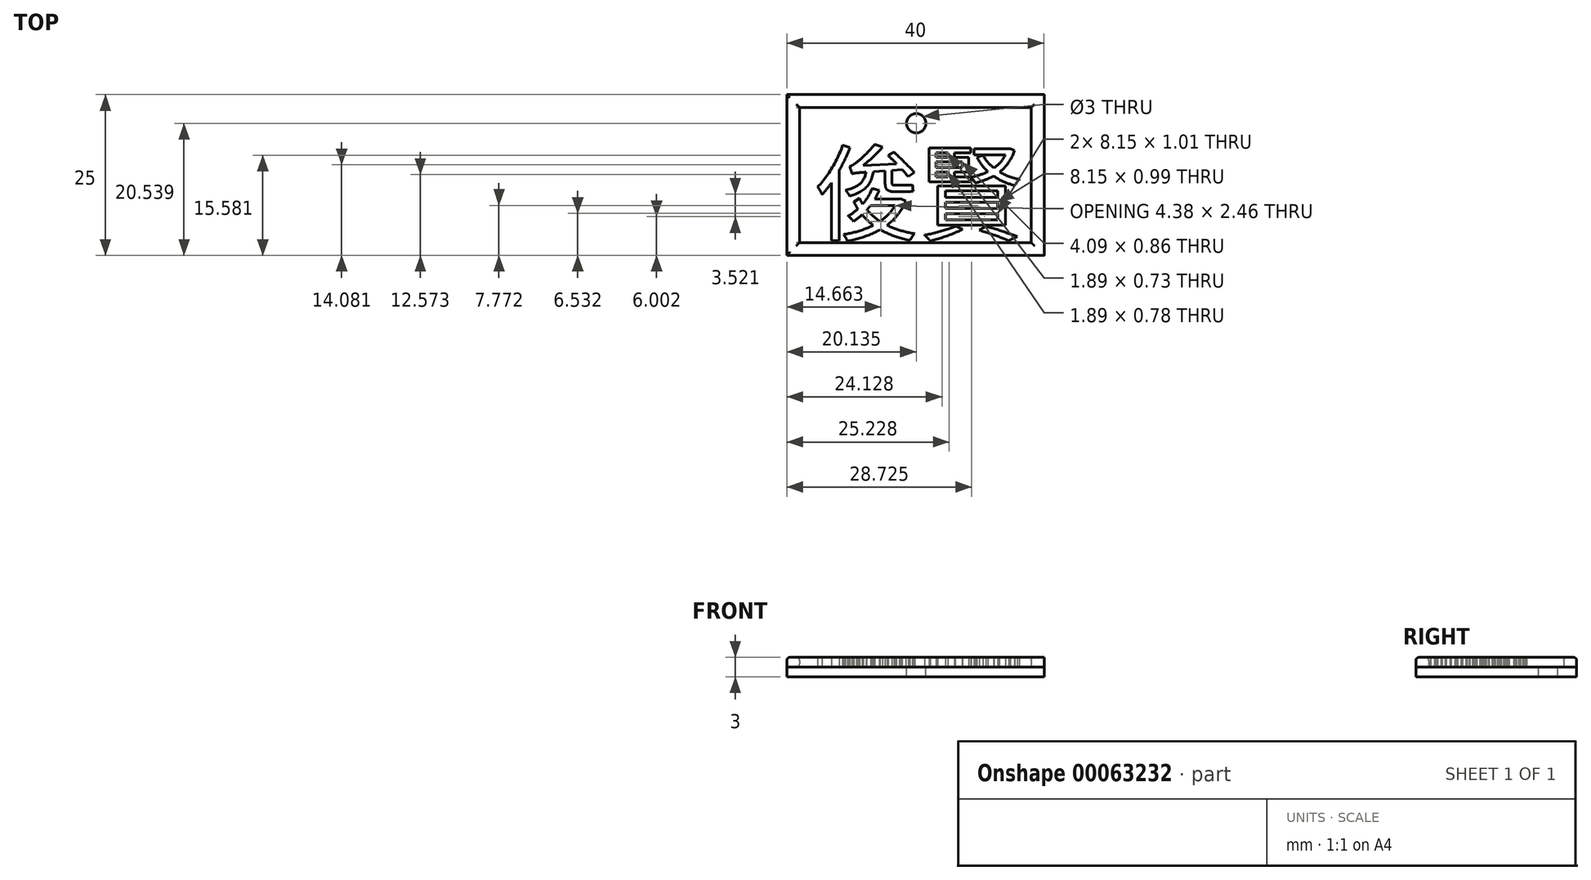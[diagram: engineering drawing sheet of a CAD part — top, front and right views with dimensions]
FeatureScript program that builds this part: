
annotation { "Feature Type Name" : "Feature", "Feature Type Description" : "" }
export const myFeature = defineFeature(function(context is Context, id is Id, definition is map)
    precondition{}
    {
        {
            var Q0;
            Q0=qCreatedBy(makeId("Top.planeOp"),FACE);
            var sketch = newSketch(context, id + "F0", { "sketchPlane" : qUnion([Q0])});
            skLineSegment(sketch, "E0.bottom", {"start": v(-19.7, 12.4) * mm, "end": v(20.3, 12.4) * mm});
            skLineSegment(sketch, "E0.top", {"start": v(-19.7, -12.6) * mm, "end": v(20.3, -12.6) * mm});
            skLineSegment(sketch, "E0.left", {"start": v(-19.7, 12.4) * mm, "end": v(-19.7, -12.6) * mm});
            skLineSegment(sketch, "E0.right", {"start": v(20.3, 12.4) * mm, "end": v(20.3, -12.6) * mm});
            skSolve(sketch);
        }
        {
            var Q0;
            Q0 = qSketchRegion(id + "F0", true);
            extrude(context, id + "F1", {"entities" : qUnion([Q0]), "depth" : 1.5 * mm});
        }
        {
            var Q0;
            Q0=makeQuery(id+"F1.opExtrude","CAP_FACE",FACE,{"disambiguationData":[OSD([sQuery(id+"F0.wireOp",EDGE,"E0.bottom"),sQuery(id+"F0.wireOp",EDGE,"E0.top"),sQuery(id+"F0.wireOp",EDGE,"E0.left"),sQuery(id+"F0.wireOp",EDGE,"E0.right")])],"isStart":false});
            var sketch = newSketch(context, id + "F2", { "sketchPlane" : qUnion([Q0])});
            skLineSegment(sketch, "E1.bottom", {"start": v(-19.7, 12.4) * mm, "end": v(20.3, 12.4) * mm});
            skLineSegment(sketch, "E1.top", {"start": v(-19.7, -12.6) * mm, "end": v(20.3, -12.6) * mm});
            skLineSegment(sketch, "E1.left", {"start": v(-19.7, 12.4) * mm, "end": v(-19.7, -12.6) * mm});
            skLineSegment(sketch, "E1.right", {"start": v(20.3, 12.4) * mm, "end": v(20.3, -12.6) * mm});
            skLineSegment(sketch, "E2.0", {"start": v(-17.7, 10.4) * mm, "end": v(18.3, 10.4) * mm});
            skLineSegment(sketch, "E2.1", {"start": v(-17.7, 10.4) * mm, "end": v(-17.7, -10.6) * mm});
            skLineSegment(sketch, "E2.2", {"start": v(-17.7, -10.6) * mm, "end": v(18.3, -10.6) * mm});
            skLineSegment(sketch, "E2.3", {"start": v(18.3, 10.4) * mm, "end": v(18.3, -10.6) * mm});
            skSolve(sketch);
        }
        {
            var Q0;
            Q0 = qSketchRegion(id + "F2", true);
            extrude(context, id + "F3", {"entities" : qUnion([Q0]), "depth" : 1.5 * mm});
        }
        {
            var Q0;
            Q0=makeQuery(id+"F1.opExtrude","CAP_FACE",FACE,{"disambiguationData":[OSD([sQuery(id+"F0.wireOp",EDGE,"E0.bottom"),sQuery(id+"F0.wireOp",EDGE,"E0.top"),sQuery(id+"F0.wireOp",EDGE,"E0.left"),sQuery(id+"F0.wireOp",EDGE,"E0.right")])],"isStart":false});
            var sketch = newSketch(context, id + "F4", { "sketchPlane" : qUnion([Q0])});
            skText(sketch, "E3", { "text": "俊賢", "fontName": "NotoSansCJKtc-Regular.otf"});
            const initialGuessF4  = {"E3": [-0.01554, -0.00906, 1, 0, 0.01174]};
            skSetInitialGuess(sketch, initialGuessF4);
            skSolve(sketch);
        }
        {
            var Q0;
            Q0 = qSketchRegion(id + "F4", true);
            extrude(context, id + "F5", {"entities" : qUnion([Q0]), "depth" : 1.5 * mm});
        }
        {
            var Q0;
            Q0=makeQuery(id+"F1.opExtrude","CAP_FACE",FACE,{"disambiguationData":[OSD([sQuery(id+"F0.wireOp",EDGE,"E0.bottom"),sQuery(id+"F0.wireOp",EDGE,"E0.top"),sQuery(id+"F0.wireOp",EDGE,"E0.left"),sQuery(id+"F0.wireOp",EDGE,"E0.right")])],"isStart":false});
            var sketch = newSketch(context, id + "F6", { "sketchPlane" : qUnion([Q0])});
            skCircle(sketch, "E4", {"center": v(0.43, 7.94) * mm, "radius": 1.5 * mm});
            skSolve(sketch);
        }
        {
            var Q0;
            Q0 = qSketchRegion(id + "F6", true);
            extrude(context, id + "F7", {"entities" : qUnion([Q0]), "operationType" : NewBodyOperationType.REMOVE, "oppositeDirection" : true, "depth" : 25 * mm});
        }
        {
            var Q0;
            Q0=makeQuery(id+"F3.opExtrude","CAP_EDGE",EDGE,{"disambiguationData":[OSD([sQuery(id+"F2.wireOp",EDGE,"E1.bottom")])],"isStart":false});
            var Q1;
            Q1=makeQuery(id+"F3.opExtrude","CAP_EDGE",EDGE,{"disambiguationData":[OSD([sQuery(id+"F2.wireOp",EDGE,"E1.top")])],"isStart":false});
            var Q2;
            Q2=makeQuery(id+"F3.opExtrude","CAP_EDGE",EDGE,{"disambiguationData":[OSD([sQuery(id+"F2.wireOp",EDGE,"E1.left")])],"isStart":false});
            var Q3;
            Q3=makeQuery(id+"F3.opExtrude","CAP_EDGE",EDGE,{"disambiguationData":[OSD([sQuery(id+"F2.wireOp",EDGE,"E2.1")])],"isStart":true});
            var Q4;
            Q4=makeQuery(id+"F3.opExtrude","CAP_EDGE",EDGE,{"disambiguationData":[OSD([sQuery(id+"F2.wireOp",EDGE,"E2.2")])],"isStart":false});
            var Q5;
            Q5=makeQuery(id+"F3.opExtrude","CAP_EDGE",EDGE,{"disambiguationData":[OSD([sQuery(id+"F2.wireOp",EDGE,"E2.0")])],"isStart":false});
            var Q6;
            Q6=makeQuery(id+"F3.opExtrude","CAP_EDGE",EDGE,{"disambiguationData":[OSD([sQuery(id+"F2.wireOp",EDGE,"E2.1")])],"isStart":false});
            var Q7;
            Q7=makeQuery(id+"F3.opExtrude","CAP_EDGE",EDGE,{"disambiguationData":[OSD([sQuery(id+"F2.wireOp",EDGE,"E2.3")])],"isStart":false});
            fillet(context, id + "F8", {"entities" : qUnion([Q0, Q1, Q2, Q3, Q4, Q5, Q6, Q7]), "radius" : 0.5 * mm, "tangentPropagation" : true, "allowEdgeOverflow" : false});
        }
    });
